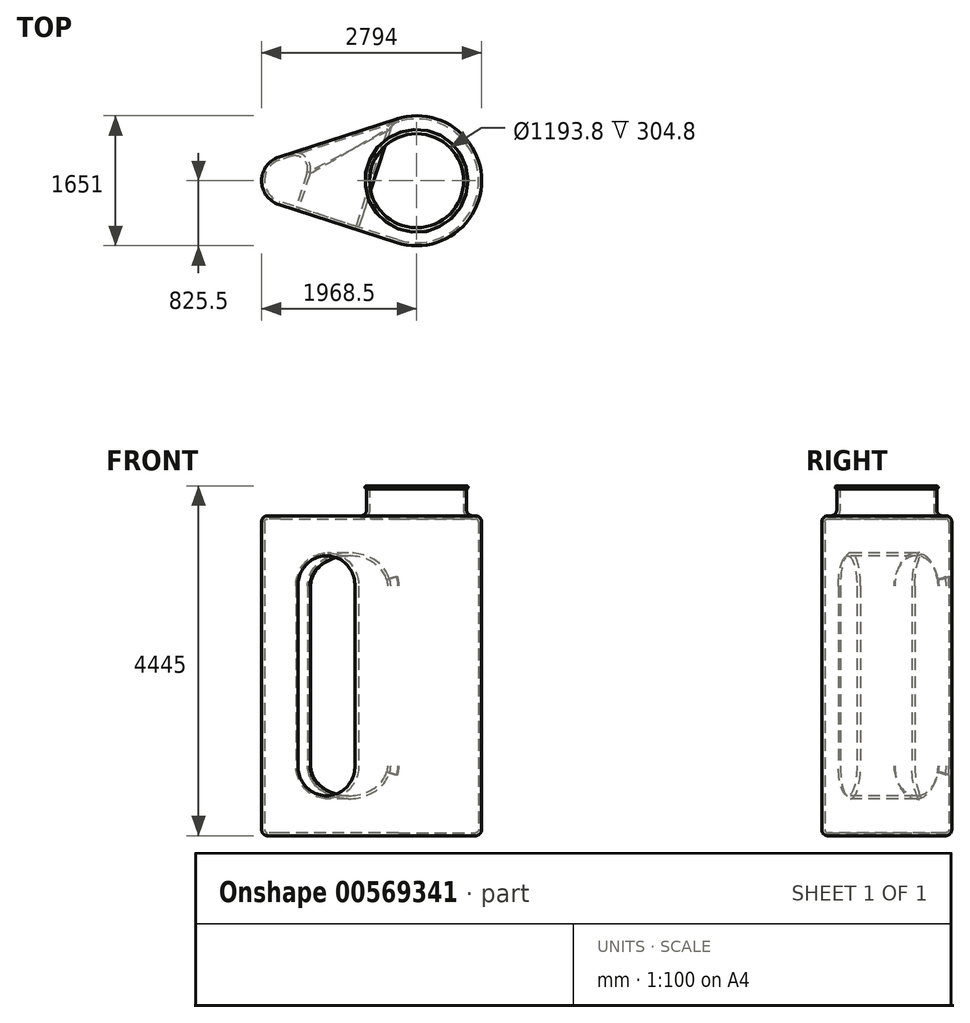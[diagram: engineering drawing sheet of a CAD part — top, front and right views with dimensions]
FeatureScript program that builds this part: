
annotation { "Feature Type Name" : "Feature", "Feature Type Description" : "" }
export const myFeature = defineFeature(function(context is Context, id is Id, definition is map)
    precondition{}
    {
        {
            var Q0;
            Q0=qCreatedBy(makeId("Top.planeOp"),FACE);
            var sketch = newSketch(context, id + "F0", { "sketchPlane" : qUnion([Q0])});
            skArc(sketch, "E0", {"start": v(-254, -785.45) * mm, "mid": v(825.5, 0) * mm, "end": v(-254, 785.45) * mm});
            skArc(sketch, "E1", {"start": v(-1748.7, 302.1) * mm, "mid": v(-1968.5, 0) * mm, "end": v(-1748.7, -302.1) * mm});
            skLineSegment(sketch, "E2", {"start": v(-1748.7, 302.1) * mm, "end": v(-254, 785.45) * mm});
            skLineSegment(sketch, "E3", {"start": v(-1748.7, -302.1) * mm, "end": v(-254, -785.45) * mm});
            skSolve(sketch);
        }
        {
            var Q0;
            Q0=makeQuery(id+"F0.imprint","IMPRINT",FACE,{"disambiguationData":[TD([[makeQuery(id+"F0.imprint","IMPRINT",EDGE,{"derivedFrom":sQuery(id+"F0.wireOp",EDGE,"E0")}),1.0]])]});
            extrude(context, id + "F1", {"entities" : qUnion([Q0]), "depth" : 4064 * mm, "offsetDistance" : 25.4 * mm});
        }
        {
            var Q0;
            Q0=makeQuery(id+"F1.opExtrude","SWEPT_FACE",FACE,{"disambiguationData":[OSD([sQuery(id+"F0.wireOp",EDGE,"E3")])]});
            var sketch = newSketch(context, id + "F2", { "sketchPlane" : qUnion([Q0])});
            skArc(sketch, "E4", {"start": v(-554.9, 3175) * mm, "mid": v(-935.9, 3556) * mm, "end": v(-1316.9, 3175) * mm});
            skArc(sketch, "E5", {"start": v(-1316.9, 889) * mm, "mid": v(-935.9, 508) * mm, "end": v(-554.9, 889) * mm});
            skLineSegment(sketch, "E6", {"start": v(-1316.9, 3175) * mm, "end": v(-1316.9, 889) * mm});
            skLineSegment(sketch, "E7", {"start": v(-554.9, 3175) * mm, "end": v(-554.9, 889) * mm});
            skSolve(sketch);
        }
        {
            var Q0;
            Q0=makeQuery(id+"F2.imprint","IMPRINT",FACE,{"disambiguationData":[TD([[makeQuery(id+"F2.imprint","IMPRINT",EDGE,{"derivedFrom":sQuery(id+"F2.wireOp",EDGE,"E4")}),1.0]])]});
            extrude(context, id + "F3", {"entities" : qUnion([Q0]), "operationType" : NewBodyOperationType.REMOVE, "endBound" : BoundingType.THROUGH_ALL, "oppositeDirection" : true, "depth" : 25.4 * mm, "offsetDistance" : 25.4 * mm});
        }
        {
            var Q0;
            Q0=makeQuery(id+"F1.opExtrude","CAP_FACE",FACE,{"disambiguationData":[OSD([sQuery(id+"F0.wireOp",EDGE,"E0"),sQuery(id+"F0.wireOp",EDGE,"E1"),sQuery(id+"F0.wireOp",EDGE,"E2"),sQuery(id+"F0.wireOp",EDGE,"E3")])],"isStart":false});
            var sketch = newSketch(context, id + "F4", { "sketchPlane" : qUnion([Q0])});
            skCircle(sketch, "E8", {"center": v(0, 0) * mm, "radius": 635 * mm});
            skSolve(sketch);
        }
        {
            var Q0;
            Q0 = qSketchRegion(id + "F4", true);
            extrude(context, id + "F5", {"entities" : qUnion([Q0]), "operationType" : NewBodyOperationType.ADD, "depth" : 381 * mm, "offsetDistance" : 25.4 * mm});
        }
        {
            var Q0;
            Q0=makeQuery(id+"F3.boolean.opBoolean","INTERSECT",EDGE,{"derivedFrom":[makeQuery(id+"F1.opExtrude","SWEPT_FACE",FACE,{"disambiguationData":[OSD([sQuery(id+"F0.wireOp",EDGE,"E2")])]}),makeQuery(id+"F3.opExtrude","SWEPT_FACE",FACE,{"disambiguationData":[OSD([sQuery(id+"F2.wireOp",EDGE,"E6")])]})]});
            var Q1;
            Q1=makeQuery(id+"F3.boolean.opBoolean","COPY",EDGE,{"derivedFrom":makeQuery(id+"F3.opExtrude","CAP_EDGE",EDGE,{"disambiguationData":[OSD([sQuery(id+"F2.wireOp",EDGE,"E6")])],"isStart":true})});
            fillet(context, id + "F6", {"entities" : qUnion([Q0, Q1]), "radius" : 203.2 * mm, "tangentPropagation" : true, "allowEdgeOverflow" : false});
        }
        {
            var Q0;
            Q0=makeQuery(id+"F1.opExtrude","CAP_FACE",FACE,{"disambiguationData":[OSD([sQuery(id+"F0.wireOp",EDGE,"E0"),sQuery(id+"F0.wireOp",EDGE,"E1"),sQuery(id+"F0.wireOp",EDGE,"E2"),sQuery(id+"F0.wireOp",EDGE,"E3")])],"isStart":false});
            var Q1;
            Q1=makeQuery(id+"F1.opExtrude","CAP_EDGE",EDGE,{"disambiguationData":[OSD([sQuery(id+"F0.wireOp",EDGE,"E0")])],"isStart":true});
            fillet(context, id + "F7", {"entities" : qUnion([Q0, Q1]), "radius" : 76.2 * mm, "tangentPropagation" : true, "allowEdgeOverflow" : false});
        }
        {
            var Q0;
            Q0=makeQuery(id+"F5.opExtrude","CAP_FACE",FACE,{"disambiguationData":[OSD([sQuery(id+"F4.wireOp",EDGE,"E8")])],"isStart":false});
            shell(context, id + "F8", {"entities" : qUnion([Q0]), "thickness" : 38.1 * mm});
        }
        {
            var Q0;
            Q0=qCreatedBy(makeId("Front.planeOp"),FACE);
            var sketch = newSketch(context, id + "F9", { "sketchPlane" : qUnion([Q0])});
            skLineSegment(sketch, "E9", {"start": v(635, 4590.54) * mm, "end": v(635, 3917.8) * mm, "construction": true});
            skLineSegment(sketch, "E10", {"start": v(0, 4569.37) * mm, "end": v(0, 3867.91) * mm, "construction": true});
            skArc(sketch, "E11", {"start": v(635, 4406.9) * mm, "mid": v(654.05, 4425.95) * mm, "end": v(635, 4445) * mm});
            skLineSegment(sketch, "E12", {"start": v(635, 4445) * mm, "end": v(635, 4406.9) * mm});
            skSolve(sketch);
        }
        {
            var Q0;
            Q0=makeQuery(id+"F9.imprint","IMPRINT",FACE,{"disambiguationData":[TD([[makeQuery(id+"F9.imprint","IMPRINT",EDGE,{"derivedFrom":sQuery(id+"F9.wireOp",EDGE,"E11")}),1.0]])]});
            var Q1;
            Q1=sQuery(id+"F9.wireOp",EDGE,"E10");
            revolve(context, id + "F10", {"operationType" : NewBodyOperationType.ADD, "entities" : qUnion([Q0]), "axis" : qUnion([Q1]), "revolveType" : RevolveType.FULL});
        }
    });
